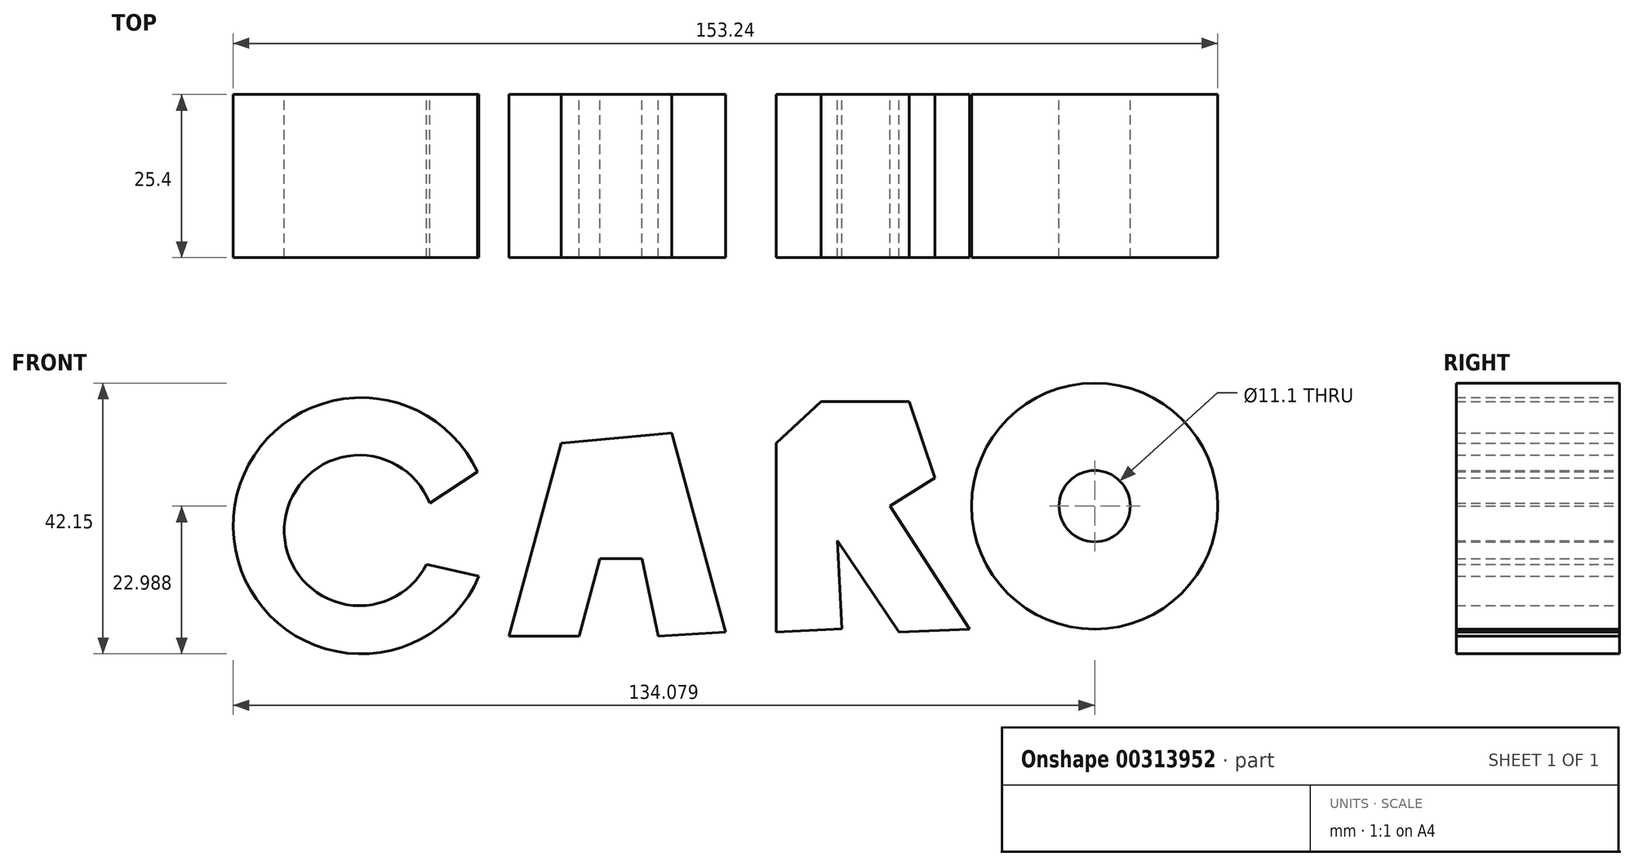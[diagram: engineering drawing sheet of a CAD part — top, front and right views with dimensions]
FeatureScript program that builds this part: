
annotation { "Feature Type Name" : "Feature", "Feature Type Description" : "" }
export const myFeature = defineFeature(function(context is Context, id is Id, definition is map)
    precondition{}
    {
        {
            var Q0;
            Q0=qCreatedBy(makeId("Front.planeOp"),FACE);
            var sketch = newSketch(context, id + "F0", { "sketchPlane" : qUnion([Q0])});
            skArc(sketch, "E0", {"start": v(-38.6, 20.47) * mm, "mid": v(-76.63, 11.78) * mm, "end": v(-38.38, 4.19) * mm});
            skArc(sketch, "E1", {"start": v(-46.05, 15.58) * mm, "mid": v(-68.68, 11.9) * mm, "end": v(-46.52, 6.05) * mm});
            skLineSegment(sketch, "E2", {"start": v(-46.05, 15.58) * mm, "end": v(-38.6, 20.47) * mm});
            skLineSegment(sketch, "E3", {"start": v(-46.52, 6.05) * mm, "end": v(-38.38, 4.19) * mm});
            skLineSegment(sketch, "E4", {"start": v(-25.58, 24.89) * mm, "end": v(-33.73, -5.12) * mm});
            skLineSegment(sketch, "E5", {"start": v(-33.73, -5.12) * mm, "end": v(-22.8, -5.12) * mm});
            skLineSegment(sketch, "E6", {"start": v(-22.8, -5.12) * mm, "end": v(-19.54, 6.98) * mm});
            skLineSegment(sketch, "E7", {"start": v(-19.54, 6.98) * mm, "end": v(-13.02, 6.98) * mm});
            skLineSegment(sketch, "E8", {"start": v(-13.02, 6.98) * mm, "end": v(-10.47, -5.12) * mm});
            skLineSegment(sketch, "E9", {"start": v(-10.47, -5.12) * mm, "end": v(0, -4.48) * mm});
            skLineSegment(sketch, "E10", {"start": v(0, -4.48) * mm, "end": v(-8.37, 26.51) * mm});
            skLineSegment(sketch, "E11", {"start": v(-8.37, 26.51) * mm, "end": v(-25.58, 24.89) * mm});
            skLineSegment(sketch, "E12", {"start": v(7.9, 24.89) * mm, "end": v(7.9, -4.48) * mm});
            skLineSegment(sketch, "E13", {"start": v(7.9, -4.48) * mm, "end": v(18.12, -3.94) * mm});
            skLineSegment(sketch, "E14", {"start": v(18.12, -3.94) * mm, "end": v(17.4, 9.77) * mm});
            skLineSegment(sketch, "E15", {"start": v(17.4, 9.77) * mm, "end": v(26.98, -4.48) * mm});
            skLineSegment(sketch, "E16", {"start": v(26.98, -4.48) * mm, "end": v(37.95, -4.04) * mm});
            skLineSegment(sketch, "E17", {"start": v(25.58, 15.12) * mm, "end": v(37.95, -4.04) * mm});
            skLineSegment(sketch, "E18", {"start": v(7.9, 24.89) * mm, "end": v(14.89, 31.4) * mm});
            skLineSegment(sketch, "E19", {"start": v(14.89, 31.4) * mm, "end": v(28.6, 31.4) * mm});
            skLineSegment(sketch, "E20", {"start": v(28.6, 31.4) * mm, "end": v(32.56, 19.54) * mm});
            skLineSegment(sketch, "E21", {"start": v(32.56, 19.54) * mm, "end": v(25.58, 15.12) * mm});
            skCircle(sketch, "E22", {"center": v(57.45, 15.12) * mm, "radius": 19.16 * mm});
            skCircle(sketch, "E23", {"center": v(57.45, 15.12) * mm, "radius": 5.55 * mm});
            skSolve(sketch);
        }
        {
            var Q0;
            Q0=makeQuery(id+"F0.imprint","IMPRINT",FACE,{"disambiguationData":[TD([[makeQuery(id+"F0.imprint","IMPRINT",EDGE,{"derivedFrom":sQuery(id+"F0.wireOp",EDGE,"E0")}),1.0]])]});
            var Q1;
            Q1=makeQuery(id+"F0.imprint","IMPRINT",FACE,{"disambiguationData":[TD([[makeQuery(id+"F0.imprint","IMPRINT",EDGE,{"derivedFrom":sQuery(id+"F0.wireOp",EDGE,"E12")}),1.0]])]});
            var Q2;
            Q2=makeQuery(id+"F0.imprint","IMPRINT",FACE,{"disambiguationData":[TD([[makeQuery(id+"F0.imprint","IMPRINT",EDGE,{"derivedFrom":sQuery(id+"F0.wireOp",EDGE,"E22")}),1.0]])]});
            var Q3;
            Q3=makeQuery(id+"F0.imprint","IMPRINT",FACE,{"disambiguationData":[TD([[makeQuery(id+"F0.imprint","IMPRINT",EDGE,{"derivedFrom":sQuery(id+"F0.wireOp",EDGE,"E4")}),1.0]])]});
            extrude(context, id + "F1", {"entities" : qUnion([Q0, Q1, Q2, Q3]), "depth" : 25.4 * mm});
        }
    });
